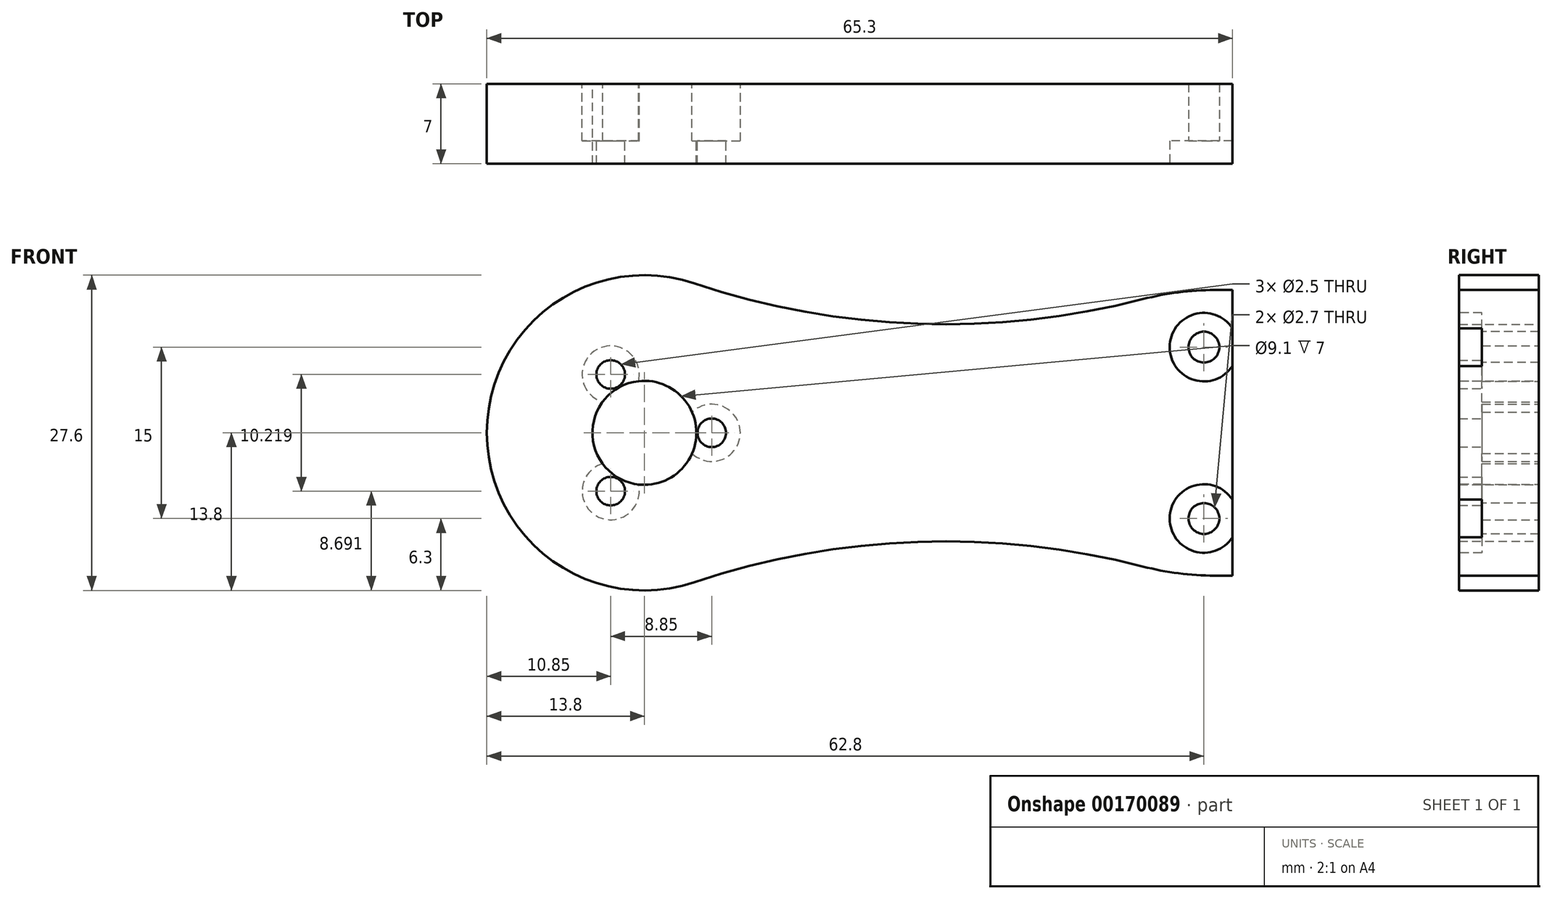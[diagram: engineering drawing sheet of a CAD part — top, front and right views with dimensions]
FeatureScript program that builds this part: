
annotation { "Feature Type Name" : "Feature", "Feature Type Description" : "" }
export const myFeature = defineFeature(function(context is Context, id is Id, definition is map)
    precondition{}
    {
        {
            var Q0;
            Q0=qCreatedBy(makeId("Front.planeOp"),FACE);
            var sketch = newSketch(context, id + "F0", { "sketchPlane" : qUnion([Q0])});
            skCircle(sketch, "E0", {"center": v(0, 0) * mm, "radius": 5.9 * mm, "construction": true});
            skCircle(sketch, "E1", {"center": v(0, 0) * mm, "radius": 13.8 * mm});
            skLineSegment(sketch, "E2", {"start": v(49, 7.5) * mm, "end": v(49, -7.5) * mm, "construction": true});
            skLineSegment(sketch, "E3", {"start": v(0, 0) * mm, "end": v(49, 0) * mm, "construction": true});
            skLineSegment(sketch, "E4", {"start": v(0, 0) * mm, "end": v(-2.95, 5.1) * mm, "construction": true});
            skLineSegment(sketch, "E5", {"start": v(0, 0) * mm, "end": v(-2.95, -5.1) * mm, "construction": true});
            skCircle(sketch, "E6", {"center": v(0, 0) * mm, "radius": 4.55 * mm});
            skLineSegment(sketch, "E7", {"start": v(51.5, 12.5) * mm, "end": v(51.5, -12.5) * mm});
            skLineSegment(sketch, "E8", {"start": v(51.5, -12.5) * mm, "end": v(46.5, -12.5) * mm});
            skLineSegment(sketch, "E9", {"start": v(46.5, 12.5) * mm, "end": v(51.5, 12.5) * mm});
            skLineSegment(sketch, "E10", {"start": v(49, 7.5) * mm, "end": v(49, 12.5) * mm, "construction": true});
            skPoint(sketch, "E11", {"position": v(-2.95, 5.1) * mm});
            skPoint(sketch, "E12", {"position": v(-2.95, -5.1) * mm});
            skPoint(sketch, "E13", {"position": v(5.9, 0) * mm});
            skPoint(sketch, "E14", {"position": v(49, 7.5) * mm});
            skPoint(sketch, "E15", {"position": v(49, -7.5) * mm});
            skArc(sketch, "E16", {"start": v(4.39, 13.08) * mm, "mid": v(25.4, 9.5) * mm, "end": v(46.5, 12.5) * mm});
            skArc(sketch, "E17.MirrorCS", {"start": v(4.39, -13.08) * mm, "mid": v(25.4, -9.5) * mm, "end": v(46.5, -12.5) * mm});
            skSolve(sketch);
        }
        {
            var Q0;
            Q0=makeQuery(id+"F0.imprint","IMPRINT",FACE,{"disambiguationData":[TD([[makeQuery(id+"F0.imprint","IMPRINT",EDGE,{"derivedFrom":sQuery(id+"F0.wireOp",EDGE,"E6")}),-1.0]])]});
            var Q1;
            Q1=makeQuery(id+"F0.imprint","IMPRINT",FACE,{"disambiguationData":[TD([[makeQuery(id+"F0.imprint","IMPRINT",EDGE,{"derivedFrom":sQuery(id+"F0.wireOp",EDGE,"E7")}),-1.0]])]});
            extrude(context, id + "F1", {"entities" : qUnion([Q0, Q1]), "depth" : 7 * mm});
        }
        {
            var Q0;
            Q0=makeQuery(id+"F1.opExtrude","CAP_FACE",FACE,{"disambiguationData":[OSD([sQuery(id+"F0.wireOp",EDGE,"E1"),sQuery(id+"F0.wireOp",EDGE,"E6"),sQuery(id+"F0.wireOp",EDGE,"E7"),sQuery(id+"F0.wireOp",EDGE,"E8"),sQuery(id+"F0.wireOp",EDGE,"E9"),sQuery(id+"F0.wireOp",EDGE,"E16"),sQuery(id+"F0.wireOp",EDGE,"E17.MirrorCS")])],"isStart":false});
            var sketch = newSketch(context, id + "F2", { "sketchPlane" : qUnion([Q0])});
            skPoint(sketch, "E18", {"position": v(49, 7.5) * mm});
            skPoint(sketch, "E19", {"position": v(49, -7.5) * mm});
            skSolve(sketch);
        }
        {
            var Q0;
            Q0=sQuery(id+"F0.wireOp",VERTEX,"E11");
            var Q1;
            Q1=sQuery(id+"F0.wireOp",VERTEX,"E12");
            var Q2;
            Q2=sQuery(id+"F0.wireOp",VERTEX,"E13");
            var Q3;
            Q3=makeQuery(id+"F1.opExtrude","SWEPT_BODY",BODY,{"disambiguationData":[OSD([sQuery(id+"F0.wireOp",EDGE,"E1"),sQuery(id+"F0.wireOp",EDGE,"E6"),sQuery(id+"F0.wireOp",EDGE,"E7"),sQuery(id+"F0.wireOp",EDGE,"E8"),sQuery(id+"F0.wireOp",EDGE,"E9"),sQuery(id+"F0.wireOp",EDGE,"E16"),sQuery(id+"F0.wireOp",EDGE,"E17.MirrorCS")])]});
            hole(context, id + "F3", {"style" : HoleStyle.C_BORE, "endStyle" : HoleEndStyle.THROUGH, "oppositeDirection" : true, "holeDiameter" : 2.5 * mm, "cBoreDiameter" : 5 * mm, "cBoreDepth" : 5 * mm, "locations" : qUnion([Q0, Q1, Q2]), "scope" : qUnion([Q3]), "isTappedThrough" : true});
        }
        {
            var Q0;
            Q0=sQuery(id+"F2.wireOp",VERTEX,"E18");
            var Q1;
            Q1=sQuery(id+"F2.wireOp",VERTEX,"E19");
            var Q2;
            Q2=makeQuery(id+"F1.opExtrude","SWEPT_BODY",BODY,{"disambiguationData":[OSD([sQuery(id+"F0.wireOp",EDGE,"E1"),sQuery(id+"F0.wireOp",EDGE,"E6"),sQuery(id+"F0.wireOp",EDGE,"E7"),sQuery(id+"F0.wireOp",EDGE,"E8"),sQuery(id+"F0.wireOp",EDGE,"E9"),sQuery(id+"F0.wireOp",EDGE,"E16"),sQuery(id+"F0.wireOp",EDGE,"E17.MirrorCS")])]});
            hole(context, id + "F4", {"style" : HoleStyle.C_BORE, "endStyle" : HoleEndStyle.THROUGH, "holeDiameter" : 2.7 * mm, "cBoreDiameter" : 6 * mm, "cBoreDepth" : 2 * mm, "locations" : qUnion([Q0, Q1]), "scope" : qUnion([Q2]), "isTappedThrough" : true});
        }
        {
            var Q0;
            {var subQ0=sQuery(id+"F0.wireOp",EDGE,"E16");var subQ1=sQuery(id+"F0.wireOp",EDGE,"E9");Q0=makeQuery(id+"FfWz6EgWY9KwT2R_1.boolean.opBoolean","MERGE",EDGE,{"derivedFrom":[makeQuery(id+"F1.opExtrude","SWEPT_EDGE",EDGE,{"disambiguationData":[OSD([subQ1,subQ0])]}),makeQuery(id+"FfWz6EgWY9KwT2R_1.opExtrude","SWEPT_EDGE",EDGE,{"disambiguationData":[OSD([subQ1,subQ0])]})]});}
            var Q1;
            {var subQ0=sQuery(id+"F0.wireOp",EDGE,"E17.MirrorCS");var subQ1=sQuery(id+"F0.wireOp",EDGE,"E8");Q1=makeQuery(id+"FfWz6EgWY9KwT2R_1.boolean.opBoolean","MERGE",EDGE,{"derivedFrom":[makeQuery(id+"F1.opExtrude","SWEPT_EDGE",EDGE,{"disambiguationData":[OSD([subQ1,subQ0])]}),makeQuery(id+"FfWz6EgWY9KwT2R_1.opExtrude","SWEPT_EDGE",EDGE,{"disambiguationData":[OSD([subQ1,subQ0])]})]});}
            fillet(context, id + "F5", {"entities" : qUnion([Q0, Q1]), "radius" : 25 * mm, "tangentPropagation" : true, "allowEdgeOverflow" : false});
        }
    });
